FCSTD DOCUMENT  (FreeCAD 0.20R29177 (Git))
Label: cargotrailer_assembly
License: All rights reserved
LicenseURL: http://en.wikipedia.org/wiki/All_rights_reserved
objects: App::Link×80, App::DocumentObjectGroup×7
EXTERNAL_REF file=Items/NoBrand/Wood Frame/framefront.FCStd obj=Body
EXTERNAL_REF file=Items/NoBrand/Wood Frame/framerear.FCStd obj=Body
EXTERNAL_REF file=Items/NoBrand/Wood Frame/framesideleft.FCStd obj=Body
EXTERNAL_REF file=Items/NoBrand/Wood Frame/framecorner.FCStd obj=Body
EXTERNAL_REF file=Items/NoBrand/Wood Frame/framesideright.FCStd obj=Body
EXTERNAL_REF file=Items/UTZ/RAKO 400x300x117/RAKO 400x300x117.FCStd obj=Body
EXTERNAL_REF file=Items/IKEA/rightcornersupport.FCStd obj=Body
EXTERNAL_REF file=Items/NoBrand/Wood Frame/base.FCStd obj=Body
EXTERNAL_REF file=Items/unitec/Reflecteur avant rond/Reflecteur avant rond.FCStd obj=Body
EXTERNAL_REF file=Items/unitec/Reflecteur arriere/Reflecteur arriere.FCStd obj=Body
EXTERNAL_REF file=Items/Micro/Black Wheel 200mm/Black Wheel 200mm.FCStd obj=Body
EXTERNAL_REF file=Items/Do it Garden/Equerre 100x15x15/Equerre 100x100x15.FCStd obj=Body
EXTERNAL_REF file=Items/Do it Garden/Raccord 160x60/Raccord 160x60.FCStd obj=Body
EXTERNAL_REF file=Items/Do it Garden/Plaque de renfort 48x15/Plaque de renfort 48x15.FCStd obj=Body
EXTERNAL_REF file=Items/Do it Garden/Equerre 70x36x16/Equerre 70x36x16.FCStd obj=Body
EXTERNAL_REF file=Items/Do it Garden/Equerre 30x30x30/Equerre 30x30x30.FCStd obj=Body
EXTERNAL_REF file=Items/NoBrand/Wood Frame/hitcharmlongsection.FCStd obj=Body
EXTERNAL_REF file=Items/NoBrand/Wood Frame/hitcharmshortsection.FCStd obj=Body
EXTERNAL_REF file=Items/NoBrand/Wood Frame/hitcharmconnector.FCStd obj=Body
EXTERNAL_REF file=Items/Croozer/Hitch Arm Attachment/hitcharmattachment.FCStd obj=Body
EXTERNAL_REF file=Items/Steinco/Series316 Swivel Castor 75mm/Series316 Swivel Castor 75mm.FCStd obj=__hga0_e030_1
EXTERNAL_REF file=Items/Ayce/Connecteur plat galvanise 2x100x35/Connecteur plat galvanise 2x100x35.FCStd obj=Body
EXTERNAL_REF file=Items/NoBrand/Wood Frame/handlebarsides.FCStd obj=Body
EXTERNAL_REF file=Items/NoBrand/Wood Frame/handlebartop.FCStd obj=Body

FEATURE [App::Link] Link  label="framefront"
  LinkedObject = -> <external Items/NoBrand/Wood Frame/framefront.FCStd>#Body
FEATURE [App::Link] Link001  label="framerear"
  LinkPlacement = pos=(0,430,0) rot=(0,0,1;0rad)
  LinkedObject = -> <external Items/NoBrand/Wood Frame/framerear.FCStd>#Body
  Placement = pos=(0,430,0) rot=(0,0,1;0rad)
FEATURE [App::Link] Link002  label="framesideright"
  LinkPlacement = pos=(0,0,0) rot=(0,0,1;1.5708rad)
  LinkedObject = -> <external Items/NoBrand/Wood Frame/framesideleft.FCStd>#Body
  Placement = pos=(0,0,0) rot=(0,0,1;1.5708rad)
FEATURE [App::Link] Link003  label="framesideleft"
  LinkPlacement = pos=(330,0,0) rot=(0,0,1;1.5708rad)
  LinkedObject = -> <external Items/NoBrand/Wood Frame/framesideleft.FCStd>#Body
  Placement = pos=(330,0,0) rot=(0,0,1;1.5708rad)
FEATURE [App::Link] Link004  label="framecorner"
  LinkPlacement = pos=(-30,0,30) rot=(0,0,1;0rad)
  LinkedObject = -> <external Items/NoBrand/Wood Frame/framecorner.FCStd>#Body
  Placement = pos=(-30,0,30) rot=(0,0,1;0rad)
FEATURE [App::Link] Link005  label="framecorner001"
  LinkPlacement = pos=(300,0,30) rot=(0,0,1;0rad)
  LinkedObject = -> Link004
  Placement = pos=(300,0,30) rot=(0,0,1;0rad)
FEATURE [App::Link] Link006  label="framecorner002"
  LinkPlacement = pos=(-30,430,30) rot=(0,0,1;0rad)
  LinkedObject = -> Link005
  Placement = pos=(-30,430,30) rot=(0,0,1;0rad)
FEATURE [App::Link] Link007  label="framecorner003"
  LinkPlacement = pos=(300,430,30) rot=(0,0,1;0rad)
  LinkedObject = -> Link006
  Placement = pos=(300,430,30) rot=(0,0,1;0rad)
FEATURE [App::Link] Link008  label="framesideright001"
  LinkPlacement = pos=(0,0,190) rot=(0,0,1;1.5708rad)
  LinkedObject = -> <external Items/NoBrand/Wood Frame/framesideright.FCStd>#Body
  Placement = pos=(0,0,190) rot=(0,0,1;1.5708rad)
FEATURE [App::Link] Link009  label="framesideright002"
  LinkPlacement = pos=(330,0,190) rot=(0,0,1;1.5708rad)
  LinkedObject = -> Link008
  Placement = pos=(330,0,190) rot=(0,0,1;1.5708rad)
FEATURE [App::Link] Link010  label="framerear001"
  LinkPlacement = pos=(0,0,190) rot=(0,0,1;0rad)
  LinkedObject = -> <external Items/NoBrand/Wood Frame/framerear.FCStd>#Body
  Placement = pos=(0,0,190) rot=(0,0,1;0rad)
FEATURE [App::Link] Link011  label="framerear002"
  LinkPlacement = pos=(0,430,190) rot=(0,0,1;0rad)
  LinkedObject = -> Link010
  Placement = pos=(0,430,190) rot=(0,0,1;0rad)
FEATURE [App::Link] Link012  label="framecorner004"
  LinkPlacement = pos=(70,0,30) rot=(0,0,1;0rad)
  LinkedObject = -> <external Items/NoBrand/Wood Frame/framecorner.FCStd>#Body
  Placement = pos=(70,0,30) rot=(0,0,1;0rad)
FEATURE [App::Link] Link013  label="framecorner005"
  LinkPlacement = pos=(70,430,30) rot=(0,0,1;0rad)
  LinkedObject = -> Link012
  Placement = pos=(70,430,30) rot=(0,0,1;0rad)
FEATURE [App::Link] Link014  label="framecorner006"
  LinkPlacement = pos=(-30,190,30) rot=(0,0,1;0rad)
  LinkedObject = -> Link013
  Placement = pos=(-30,190,30) rot=(0,0,1;0rad)
FEATURE [App::Link] Link015  label="framecorner007"
  LinkPlacement = pos=(300,190,30) rot=(0,0,1;0rad)
  LinkedObject = -> Link014
  Placement = pos=(300,190,30) rot=(0,0,1;0rad)
FEATURE [App::Link] Link016  label="Rako box"
  LinkPlacement = pos=(300,30,0) rot=(0,0,1;1.5708rad)
  LinkedObject = -> <external Items/UTZ/RAKO 400x300x117/RAKO 400x300x117.FCStd>#Body
  Placement = pos=(300,30,0) rot=(0,0,1;1.5708rad)
FEATURE [App::Link] Link017  label="rightcornersupport"
  LinkPlacement = pos=(0,0,30) rot=(0,0,1;0rad)
  LinkedObject = -> <external Items/IKEA/rightcornersupport.FCStd>#Body
  Placement = pos=(0,0,30) rot=(0,0,1;0rad)
FEATURE [App::Link] Link018  label="rightcornersupport001"
  LinkPlacement = pos=(255,0,30) rot=(0,0,1;0rad)
  LinkedObject = -> Link017
  Placement = pos=(255,0,30) rot=(0,0,1;0rad)
FEATURE [App::Link] Link019  label="rightcornersupport002"
  LinkPlacement = pos=(55,461,30) rot=(0,0,1;3.14159rad)
  LinkedObject = -> Link018
  Placement = pos=(55,461,30) rot=(0,0,1;3.14159rad)
FEATURE [App::Link] Link020  label="rightcornersupport003"
  LinkPlacement = pos=(290,461,30) rot=(0,0,1;3.14159rad)
  LinkedObject = -> Link019
  Placement = pos=(290,461,30) rot=(0,0,1;3.14159rad)
FEATURE [App::Link] Link025  label="base"
  LinkPlacement = pos=(330,0,-5) rot=(0,0,1;1.5708rad)
  LinkedObject = -> <external Items/NoBrand/Wood Frame/base.FCStd>#Body
  Placement = pos=(330,0,-5) rot=(0,0,1;1.5708rad)
FEATURE [App::Link] Link026  label="rightcornersupport004"
  LinkPlacement = pos=(-30,308,-5) rot=(0.707107,0.707107,0;3.14159rad)
  LinkedObject = -> <external Items/IKEA/rightcornersupport.FCStd>#Body
  Placement = pos=(-30,308,-5) rot=(0.707107,0.707107,0;3.14159rad)
FEATURE [App::Link] Link027  label="rightcornersupport005"
  LinkPlacement = pos=(330,353,-5) rot=(0.707107,-0.707107,0;3.14159rad)
  LinkedObject = -> Link026
  Placement = pos=(330,353,-5) rot=(0.707107,-0.707107,0;3.14159rad)
FEATURE [App::Link] Link021  label="reflectorfront"
  LinkPlacement = pos=(20,-2,55) rot=(0,0,1;0rad)
  LinkedObject = -> <external Items/unitec/Reflecteur avant rond/Reflecteur avant rond.FCStd>#Body
  Placement = pos=(20,-2,55) rot=(0,0,1;0rad)
FEATURE [App::Link] Link022  label="reflectorfront001"
  LinkPlacement = pos=(280,-2,55) rot=(0,0,1;0rad)
  LinkedObject = -> Link021
  Placement = pos=(280,-2,55) rot=(0,0,1;0rad)
FEATURE [App::Link] Link023  label="reflectorrear"
  LinkPlacement = pos=(33,462,55) rot=(0,0,1;3.14159rad)
  LinkedObject = -> <external Items/unitec/Reflecteur arriere/Reflecteur arriere.FCStd>#Body
  Placement = pos=(33,462,55) rot=(0,0,1;3.14159rad)
FEATURE [App::Link] Link024  label="reflectorrear001"
  LinkPlacement = pos=(267,462,55) rot=(0,0,1;3.14159rad)
  LinkedObject = -> Link023
  Placement = pos=(267,462,55) rot=(0,0,1;3.14159rad)
FEATURE [App::DocumentObjectGroup] Group001  label="Reflectors"
  Group = -> [Link017,Link018,Link019,Link020,Link021,Link022,Link023,Link024]
FEATURE [App::Link] Link028  label="wheel200mm"
  LinkPlacement = pos=(348,330,-29) rot=(0,0,1;1.5708rad)
  LinkedObject = -> <external Items/Micro/Black Wheel 200mm/Black Wheel 200mm.FCStd>#Body
  Placement = pos=(348,330,-29) rot=(0,0,1;1.5708rad)
FEATURE [App::Link] Link029  label="wheel200mm001"
  LinkPlacement = pos=(-48,330,-29) rot=(0,0,1;-1.5708rad)
  LinkedObject = -> Link028
  Placement = pos=(-48,330,-29) rot=(0,0,1;-1.5708rad)
FEATURE [App::DocumentObjectGroup] Group002  label="Wheels"
  Group = -> [Link029,Link028,Link027,Link026]
FEATURE [App::Link] Link030  label="Corner"
  LinkPlacement = pos=(-22.5,0,7.5) rot=(0,0,1;0rad)
  LinkedObject = -> <external Items/Do it Garden/Equerre 100x15x15/Equerre 100x100x15.FCStd>#Body
  Placement = pos=(-22.5,0,7.5) rot=(0,0,1;0rad)
FEATURE [App::Link] Link031  label="Corner001"
  LinkPlacement = pos=(322.5,-1.5,7.5) rot=(0,0,1;3.14159rad)
  LinkedObject = -> Link030
  Placement = pos=(322.5,-1.5,7.5) rot=(0,0,1;3.14159rad)
FEATURE [App::Link] Link032  label="Corner002"
  LinkPlacement = pos=(-22.5,461.5,7.5) rot=(0,0,1;0rad)
  LinkedObject = -> Link031
  Placement = pos=(-22.5,461.5,7.5) rot=(0,0,1;0rad)
FEATURE [App::Link] Link033  label="Corner003"
  LinkPlacement = pos=(322.5,460,7.5) rot=(0,0,1;3.14159rad)
  LinkedObject = -> Link032
  Placement = pos=(322.5,460,7.5) rot=(0,0,1;3.14159rad)
FEATURE [App::Link] Link058  label="Do It Garden Raccord 160x60"
  LinkPlacement = pos=(330,430,30) rot=(0,0,1;1.5708rad)
  LinkedObject = -> <external Items/Do it Garden/Raccord 160x60/Raccord 160x60.FCStd>#Body
  Placement = pos=(330,430,30) rot=(0,0,1;1.5708rad)
FEATURE [App::Link] Link059  label="Do It Garden Raccord 160x061"
  LinkPlacement = pos=(298,430,30) rot=(0,0,1;1.5708rad)
  LinkedObject = -> Link058
  Placement = pos=(298,430,30) rot=(0,0,1;1.5708rad)
FEATURE [App::Link] Link060  label="Do It Garden Raccord 160x062"
  LinkPlacement = pos=(0,430,30) rot=(0,0,1;1.5708rad)
  LinkedObject = -> Link059
  Placement = pos=(0,430,30) rot=(0,0,1;1.5708rad)
FEATURE [App::Link] Link061  label="Do It Garden Raccord 160x063"
  LinkPlacement = pos=(-32,430,30) rot=(0,0,1;1.5708rad)
  LinkedObject = -> Link060
  Placement = pos=(-32,430,30) rot=(0,0,1;1.5708rad)
FEATURE [App::Link] Link062  label="Do It Garden Raccord 160x064"
  LinkPlacement = pos=(300,190,32) rot=(1,0,0;1.5708rad)
  LinkedObject = -> Link061
  Placement = pos=(300,190,32) rot=(1,0,0;1.5708rad)
FEATURE [App::Link] Link063  label="Do It Garden Raccord 160x065"
  LinkPlacement = pos=(300,190,0) rot=(1,0,0;1.5708rad)
  LinkedObject = -> Link062
  Placement = pos=(300,190,0) rot=(1,0,0;1.5708rad)
FEATURE [App::Link] Link064  label="Do it Garden Equerre 100x100x15"
  LinkPlacement = pos=(-22.5,0,212.5) rot=(0,1,0;1.5708rad)
  LinkedObject = -> <external Items/Do it Garden/Equerre 100x15x15/Equerre 100x100x15.FCStd>#Body
  Placement = pos=(-22.5,0,212.5) rot=(0,1,0;1.5708rad)
FEATURE [App::Link] Link065  label="Do it Garden Equerre 100x100x016"
  LinkPlacement = pos=(322.5,0,212.5) rot=(0,1,0;3.14159rad)
  LinkedObject = -> Link064
  Placement = pos=(322.5,0,212.5) rot=(0,1,0;3.14159rad)
FEATURE [App::Link] Link066  label="Do it Garden Equerre 100x100x017"
  LinkPlacement = pos=(-22.5,461.5,212.5) rot=(0,1,0;1.5708rad)
  LinkedObject = -> Link065
  Placement = pos=(-22.5,461.5,212.5) rot=(0,1,0;1.5708rad)
FEATURE [App::Link] Link067  label="Do it Garden Equerre 100x100x018"
  LinkPlacement = pos=(322.5,461.5,212.5) rot=(0,1,0;3.14159rad)
  LinkedObject = -> <external Items/Do it Garden/Equerre 100x15x15/Equerre 100x100x15.FCStd>#Body
  Placement = pos=(322.5,461.5,212.5) rot=(0,1,0;3.14159rad)
FEATURE [App::Link] Link072  label="framecorner008"
  LinkPlacement = pos=(200,0,30) rot=(0,0,1;0rad)
  LinkedObject = -> <external Items/NoBrand/Wood Frame/framecorner.FCStd>#Body
  Placement = pos=(200,0,30) rot=(0,0,1;0rad)
FEATURE [App::Link] Link073  label="framecorner009"
  LinkPlacement = pos=(200,430,30) rot=(0,0,1;0rad)
  LinkedObject = -> Link072
  Placement = pos=(200,430,30) rot=(0,0,1;0rad)
FEATURE [App::DocumentObjectGroup] Group  label="Wood Frame"
  Group = -> [Link,Link001,Link002,Link003,Link004,Link005,Link006,Link007,Link008,Link009,Link011,Link010,Link012,Link013,Link014,Link015,Link025,Link073,Link072]
FEATURE [App::Link] Link074  label="Do it Garden Plaque de renfort 48x15"
  LinkPlacement = pos=(78,0,6) rot=(0,0,1;0rad)
  LinkedObject = -> <external Items/Do it Garden/Plaque de renfort 48x15/Plaque de renfort 48x15.FCStd>#Body
  Placement = pos=(78,0,6) rot=(0,0,1;0rad)
FEATURE [App::Link] Link075  label="Do it Garden Plaque de renfort 48x016"
  LinkPlacement = pos=(208,0,6) rot=(0,0,1;0rad)
  LinkedObject = -> Link074
  Placement = pos=(208,0,6) rot=(0,0,1;0rad)
FEATURE [App::Link] Link076  label="Do it Garden Plaque de renfort 48x017"
  LinkPlacement = pos=(78,0,166) rot=(0,0,1;0rad)
  LinkedObject = -> Link075
  Placement = pos=(78,0,166) rot=(0,0,1;0rad)
FEATURE [App::Link] Link077  label="Do it Garden Plaque de renfort 48x018"
  LinkPlacement = pos=(208,0,166) rot=(0,0,1;0rad)
  LinkedObject = -> Link076
  Placement = pos=(208,0,166) rot=(0,0,1;0rad)
FEATURE [App::Link] Link078  label="Do it Garden Plaque de renfort 48x019"
  LinkPlacement = pos=(78,462,6) rot=(0,0,1;0rad)
  LinkedObject = -> Link077
  Placement = pos=(78,462,6) rot=(0,0,1;0rad)
FEATURE [App::Link] Link079  label="Do it Garden Plaque de renfort 48x020"
  LinkPlacement = pos=(78,462,166) rot=(0,0,1;0rad)
  LinkedObject = -> Link078
  Placement = pos=(78,462,166) rot=(0,0,1;0rad)
FEATURE [App::Link] Link080  label="Do it Garden Plaque de renfort 48x021"
  LinkPlacement = pos=(208,462,6) rot=(0,0,1;0rad)
  LinkedObject = -> Link079
  Placement = pos=(208,462,6) rot=(0,0,1;0rad)
FEATURE [App::Link] Link081  label="Do it Garden Plaque de renfort 48x022"
  LinkPlacement = pos=(208,462,166) rot=(0,0,1;0rad)
  LinkedObject = -> Link080
  Placement = pos=(208,462,166) rot=(0,0,1;0rad)
FEATURE [App::Link] Link082  label="Do it Garden Plaque de renfort 48x023"
  LinkPlacement = pos=(-32,7,166) rot=(0,0,1;1.5708rad)
  LinkedObject = -> Link081
  Placement = pos=(-32,7,166) rot=(0,0,1;1.5708rad)
FEATURE [App::Link] Link083  label="Do it Garden Plaque de renfort 48x024"
  LinkPlacement = pos=(-32,7,6) rot=(0,0,1;1.5708rad)
  LinkedObject = -> Link082
  Placement = pos=(-32,7,6) rot=(0,0,1;1.5708rad)
FEATURE [App::Link] Link084  label="Do it Garden Plaque de renfort 48x025"
  LinkPlacement = pos=(330,7,6) rot=(0,0,1;1.5708rad)
  LinkedObject = -> Link083
  Placement = pos=(330,7,6) rot=(0,0,1;1.5708rad)
FEATURE [App::Link] Link085  label="Do it Garden Plaque de renfort 48x026"
  LinkPlacement = pos=(330,7,166) rot=(0,0,1;1.5708rad)
  LinkedObject = -> Link084
  Placement = pos=(330,7,166) rot=(0,0,1;1.5708rad)
FEATURE [App::Link] Link086  label="Do it Garden Equerre 70x36x16"
  LinkPlacement = pos=(-31.5,205,11) rot=(0,0,1;1.5708rad)
  LinkedObject = -> <external Items/Do it Garden/Equerre 70x36x16/Equerre 70x36x16.FCStd>#Body
  Placement = pos=(-31.5,205,11) rot=(0,0,1;1.5708rad)
FEATURE [App::Link] Link087  label="Do it Garden Equerre 70x36x017"
  LinkPlacement = pos=(330,205,11) rot=(0,0,1;1.5708rad)
  LinkedObject = -> Link086
  Placement = pos=(330,205,11) rot=(0,0,1;1.5708rad)
FEATURE [App::Link] Link088  label="Do it Garden Equerre 70x36x018"
  LinkPlacement = pos=(-30,205,211) rot=(0.707107,0.707107,0;3.14159rad)
  LinkedObject = -> <external Items/Do it Garden/Equerre 70x36x16/Equerre 70x36x16.FCStd>#Body
  Placement = pos=(-30,205,211) rot=(0.707107,0.707107,0;3.14159rad)
FEATURE [App::Link] Link089  label="Do it Garden Equerre 70x36x019"
  LinkPlacement = pos=(331.54,205,211) rot=(0.707107,0.707107,0;3.14159rad)
  LinkedObject = -> Link088
  Placement = pos=(331.54,205,211) rot=(0.707107,0.707107,0;3.14159rad)
FEATURE [App::Link] Link090  label="Do it Garden Equerre 30x30x30"
  LinkPlacement = pos=(0,428.5,30) rot=(0,0,1;3.14159rad)
  LinkedObject = -> <external Items/Do it Garden/Equerre 30x30x30/Equerre 30x30x30.FCStd>#Body
  Placement = pos=(0,428.5,30) rot=(0,0,1;3.14159rad)
FEATURE [App::Link] Link091  label="Do it Garden Equerre 30x30x031"
  LinkPlacement = pos=(330,428.5,30) rot=(0,0,1;3.14159rad)
  LinkedObject = -> Link090
  Placement = pos=(330,428.5,30) rot=(0,0,1;3.14159rad)
FEATURE [App::Link] Link092  label="Do it Garden Equerre 30x30x032"
  LinkPlacement = pos=(-30,428.5,190) rot=(1,0,0;3.14159rad)
  LinkedObject = -> <external Items/Do it Garden/Equerre 30x30x30/Equerre 30x30x30.FCStd>#Body
  Placement = pos=(-30,428.5,190) rot=(1,0,0;3.14159rad)
FEATURE [App::Link] Link093  label="Do it Garden Equerre 30x30x033"
  LinkPlacement = pos=(300,428.5,190) rot=(1,0,0;3.14159rad)
  LinkedObject = -> Link092
  Placement = pos=(300,428.5,190) rot=(1,0,0;3.14159rad)
FEATURE [App::Link] Link094  label="hitcharmlongsection"
  LinkPlacement = pos=(332,190,0) rot=(0,0,1;0rad)
  LinkedObject = -> <external Items/NoBrand/Wood Frame/hitcharmlongsection.FCStd>#Body
  Placement = pos=(332,190,0) rot=(0,0,1;0rad)
FEATURE [App::Link] Link095  label="hitcharmshortsection"
  LinkPlacement = pos=(332,-8,0) rot=(0,0,-1;0.785398rad)
  LinkedObject = -> <external Items/NoBrand/Wood Frame/hitcharmshortsection.FCStd>#Body
  Placement = pos=(332,-8,0) rot=(0,0,-1;0.785398rad)
FEATURE [App::Link] Link096  label="hitcharmconnector"
  LinkPlacement = pos=(326,-44,0) rot=(0,0,1;3.14159rad)
  LinkedObject = -> <external Items/NoBrand/Wood Frame/hitcharmconnector.FCStd>#Body
  Placement = pos=(326,-44,0) rot=(0,0,1;3.14159rad)
FEATURE [App::Link] Link097  label="hitcharmattachment"
  LinkPlacement = pos=(178.5,-124,-2.5) rot=(0,0,1;0rad)
  LinkedObject = -> <external Items/Croozer/Hitch Arm Attachment/hitcharmattachment.FCStd>#Body
  Placement = pos=(178.5,-124,-2.5) rot=(0,0,1;0rad)
FEATURE [App::DocumentObjectGroup] Group004  label="Hitch"
  Group = -> [Link063,Link062,Link094,Link095,Link096,Link097]
FEATURE [App::Link] Link098  label="Do it Garden Plaque de renfort 48x027"
  LinkPlacement = pos=(-24,8,222) rot=(0.57735,0.57735,0.57735;2.0944rad)
  LinkedObject = -> <external Items/Do it Garden/Plaque de renfort 48x15/Plaque de renfort 48x15.FCStd>#Body
  Placement = pos=(-24,8,222) rot=(0.57735,0.57735,0.57735;2.0944rad)
FEATURE [App::Link] Link099  label="Do it Garden Plaque de renfort 48x028"
  LinkPlacement = pos=(-24,438,222) rot=(0.57735,0.57735,0.57735;2.0944rad)
  LinkedObject = -> Link098
  Placement = pos=(-24,438,222) rot=(0.57735,0.57735,0.57735;2.0944rad)
FEATURE [App::Link] Link100  label="Do it Garden Plaque de renfort 48x029"
  LinkPlacement = pos=(276,8,222) rot=(0.57735,0.57735,0.57735;2.0944rad)
  LinkedObject = -> Link099
  Placement = pos=(276,8,222) rot=(0.57735,0.57735,0.57735;2.0944rad)
FEATURE [App::Link] Link101  label="Do it Garden Plaque de renfort 48x030"
  LinkPlacement = pos=(276,438,222) rot=(0.57735,0.57735,0.57735;2.0944rad)
  LinkedObject = -> <external Items/Do it Garden/Plaque de renfort 48x15/Plaque de renfort 48x15.FCStd>#Body
  Placement = pos=(276,438,222) rot=(0.57735,0.57735,0.57735;2.0944rad)
FEATURE [App::Link] Link103  label="Series316 Swivel Castor 75mm"
  LinkPlacement = pos=(150,15,-7) rot=(0,0.707107,0.707107;3.14159rad)
  LinkedObject = -> <external Items/Steinco/Series316 Swivel Castor 75mm/Series316 Swivel Castor 75mm.FCStd>#__hga0_e030_1
  Placement = pos=(150,15,-7) rot=(0,0.707107,0.707107;3.14159rad)
FEATURE [App::DocumentObjectGroup] Group005  label="Frame Reinforcement"
  Group = -> [Link030,Link031,Link032,Link033,Link064,Link065,Link066,Link067,Link074,Link075,Link076,Link077,Link078,Link079,Link080,Link081,Link082,Link083,Link084,Link085,Link086,Link087,Link088,Link089,Link091,Link090,Link092,Link093,Link098,Link099,Link100,Link101]
FEATURE [App::Link] Link104  label="Ayce Connecteur plat galvanise 2x100x35"
  LinkPlacement = pos=(100,32.5,32) rot=(1,0,0;1.5708rad)
  LinkedObject = -> <external Items/Ayce/Connecteur plat galvanise 2x100x35/Connecteur plat galvanise 2x100x35.FCStd>#Body
  Placement = pos=(100,32.5,32) rot=(1,0,0;1.5708rad)
FEATURE [App::Link] Link105  label="Ayce Connecteur plat galvanise 2x100x036"
  LinkPlacement = pos=(100,32.5,-5) rot=(1,0,0;1.5708rad)
  LinkedObject = -> Link104
  Placement = pos=(100,32.5,-5) rot=(1,0,0;1.5708rad)
FEATURE [App::DocumentObjectGroup] Group006  label="Handcart"
  Group = -> [Link103,Link104,Link105]
FEATURE [App::Link] Link106  label="handlebarsides"
  LinkPlacement = pos=(-30,492,400) rot=(1,0,0;1.5708rad)
  LinkedObject = -> <external Items/NoBrand/Wood Frame/handlebarsides.FCStd>#Body
  Placement = pos=(-30,492,400) rot=(1,0,0;1.5708rad)
FEATURE [App::Link] Link107  label="handlebarsides001"
  LinkPlacement = pos=(300,492,400) rot=(1,0,0;1.5708rad)
  LinkedObject = -> Link106
  Placement = pos=(300,492,400) rot=(1,0,0;1.5708rad)
FEATURE [App::Link] Link108  label="hanndlebartop"
  LinkPlacement = pos=(0,462,370) rot=(0,0,1;1.5708rad)
  LinkedObject = -> <external Items/NoBrand/Wood Frame/handlebartop.FCStd>#Body
  Placement = pos=(0,462,370) rot=(0,0,1;1.5708rad)
FEATURE [App::DocumentObjectGroup] Group003  label="Handlebar"
  Group = -> [Link058,Link059,Link060,Link061,Link106,Link107,Link108]

RESOLVED EXTERNAL PARTS (link-assembly join: the EXTERNAL_REF files above that resolve inside this repo's crawl, each included once):
---- part Items/IKEA/rightcornersupport.FCStd = doc fcstd_8d029b06e237 ----
FCSTD DOCUMENT  (FreeCAD 0.20R29177 (Git))
Label: rightcornersupport
License: All rights reserved
LicenseURL: http://en.wikipedia.org/wiki/All_rights_reserved
objects: Sketcher::SketchObject×4, PartDesign::Pad×2, PartDesign::Pocket×2, PartDesign::LinearPattern×2, PartDesign::MultiTransform×1, PartDesign::Body×1
note: 16 computed .brp shape members not serialized (recipe doc carries the construction recipe); baked Part::Feature solids carry a one-line shape summary decoded from their .brp

FEATURE [Sketcher::SketchObject] Sketch
  FullyConstrained = true
  MapMode = 5
  Placement = pos=(0,0,0) rot=(1,0,0;1.5708rad)
  Support = -> [XZ_Plane]
  sketch-geometry (4):
    g0: LineSegment StartX=0 StartY=0 StartZ=0 EndX=45 EndY=0 EndZ=0
    g1: LineSegment StartX=45 StartY=0 StartZ=0 EndX=45 EndY=42 EndZ=0
    g2: LineSegment StartX=45 StartY=42 StartZ=0 EndX=0 EndY=42 EndZ=0
    g3: LineSegment StartX=0 StartY=42 StartZ=0 EndX=0 EndY=0 EndZ=0
  constraints (11):
    c: Coincident(g0,g1)
    c: Coincident(g1,g2)
    c: Coincident(g2,g3)
    c: Coincident(g3,g0)
    c: Horizontal(g0)
    c: Horizontal(g2)
    c: Vertical(g1)
    c: Vertical(g3)
    c: Coincident(g0,g-1)
    c: DistanceY(g1,g1) = 42
    c: DistanceX(g0,g0) = 45
FEATURE [PartDesign::Pad] Pad
  Direction = (1,1,1)
  Length = 1.6
  Length2 = 100
  Placement = pos=(0,0,0) rot=(1,0,0;1.5708rad)
  Profile = -> Sketch
  Type = 0
FEATURE [Sketcher::SketchObject] Sketch001
  ExternalGeometry = -> [Pad]
  FullyConstrained = true
  MapMode = 5
  Placement = pos=(0,0,0) rot=(-1,0,0;1.5708rad)
  Support = -> [Pad]
  sketch-geometry (4):
    g0: LineSegment StartX=0 StartY=0 StartZ=0 EndX=45 EndY=0 EndZ=0
    g1: LineSegment StartX=45 StartY=0 StartZ=0 EndX=45 EndY=-1.6 EndZ=0
    g2: LineSegment StartX=45 StartY=-1.6 StartZ=0 EndX=0 EndY=-1.6 EndZ=0
    g3: LineSegment StartX=0 StartY=-1.6 StartZ=0 EndX=0 EndY=0 EndZ=0
  constraints (11):
    c: Coincident(g0,g1)
    c: Coincident(g1,g2)
    c: Coincident(g2,g3)
    c: Coincident(g3,g0)
    c: Horizontal(g0)
    c: Horizontal(g2)
    c: Vertical(g1)
    c: Vertical(g3)
    c: Coincident(g0,g-1)
    c: PointOnObject(g1,g-3)
    c: DistanceY(g1,g1) = 1.6
FEATURE [PartDesign::Pad] Pad001
  BaseFeature = -> Pad
  Direction = (1,1,1)
  Length = 31
  Length2 = 100
  Placement = pos=(0,0,0) rot=(1,0,0;1.5708rad)
  Profile = -> Sketch001
  Type = 0
FEATURE [Sketcher::SketchObject] Sketch002
  ExternalGeometry = -> [Pad001]
  FullyConstrained = true
  MapMode = 5
  Placement = pos=(0,-1.6,7e-16) rot=(1,0,0;1.5708rad)
  Support = -> [Pad001]
  sketch-geometry (1):
    g0: Circle CenterX=22.5 CenterY=23.75 CenterZ=0 NormalX=0 NormalY=0 NormalZ=1 AngleXU=0 Radius=7.25
  constraints (3):
    c: Radius(g0) = 7.25
    c: DistanceY(g-1,g0) = 23.75
    c: DistanceX(g-1,g0) = 22.5
FEATURE [PartDesign::Pocket] Pocket
  BaseFeature = -> Pad001
  Direction = (1,1,1)
  Length = 5
  Length2 = 100
  Placement = pos=(0,0,0) rot=(1,0,0;1.5708rad)
  Profile = -> Sketch002
  Type = 1
FEATURE [Sketcher::SketchObject] Sketch003
  FullyConstrained = true
  MapMode = 5
  Placement = pos=(0,1.9e-15,1.6) rot=(0,0,1;3.14159rad)
  Support = -> [Pocket]
  expr: Constraints[1] = 3.3 + 3
  expr: Constraints[2] = 8.9 + 3
  sketch-geometry (1):
    g0: Circle CenterX=-6.3 CenterY=-11.9 CenterZ=0 NormalX=0 NormalY=0 NormalZ=1 AngleXU=0 Radius=3
  constraints (3):
    c: Radius(g0) = 3
    c: DistanceX(g0,g-1) = 6.3
    c: DistanceY(g0,g-1) = 11.9
FEATURE [PartDesign::Pocket] Pocket001
  BaseFeature = -> Pocket
  Direction = (1,1,1)
  Length = 5
  Length2 = 100
  Placement = pos=(0,0,0) rot=(1,0,0;1.5708rad)
  Profile = -> Sketch003
  Type = 1
FEATURE [PartDesign::LinearPattern] LinearPattern
  Direction = -> Y_Axis
  Length = 9.6
  Occurrences = 2
  Placement = pos=(0,0,0) rot=(1,0,0;1.5708rad)
  expr: Length = 3.6 + 6
FEATURE [PartDesign::LinearPattern] LinearPattern001
  Direction = -> X_Axis
  Length = 31
  Occurrences = 2
  Placement = pos=(0,0,0) rot=(1,0,0;1.5708rad)
  expr: Length = 25 + 6
FEATURE [PartDesign::MultiTransform] MultiTransform
  BaseFeature = -> Pocket001
  Originals = -> [Pocket001]
  Placement = pos=(0,0,0) rot=(1,0,0;1.5708rad)
  Transformations = -> [LinearPattern,LinearPattern001]
FEATURE [PartDesign::Body] Body  label="rightcornersupport"
  Group = -> [Sketch,Pad,Sketch001,Pad001,Sketch002,Pocket,Sketch003,Pocket001,MultiTransform,LinearPattern,LinearPattern001]
  Origin = -> Origin
  Tip = -> MultiTransform
